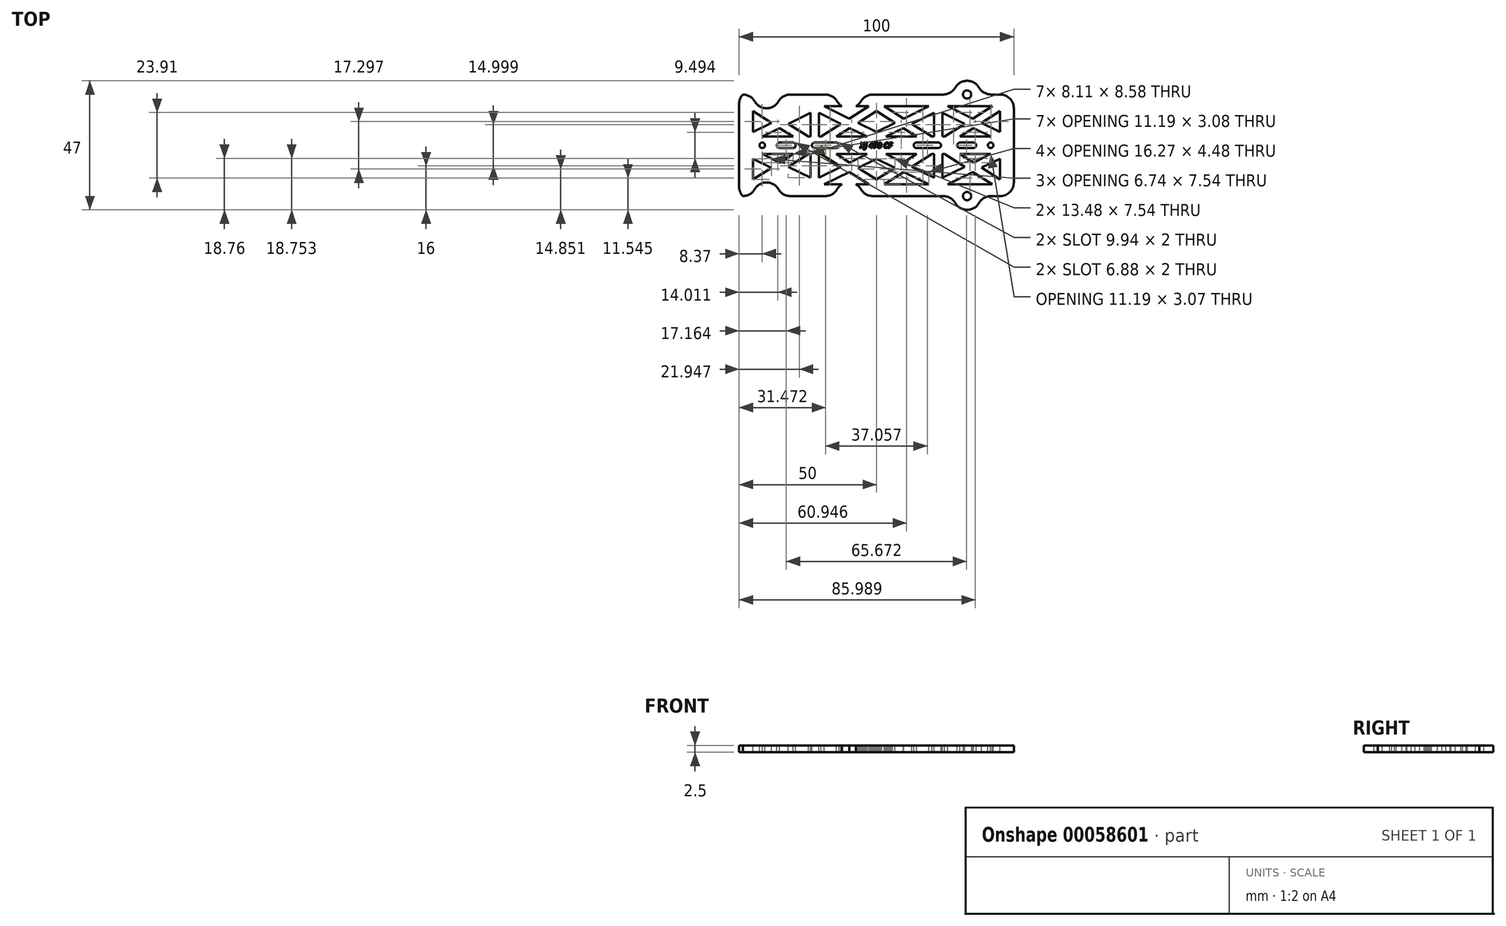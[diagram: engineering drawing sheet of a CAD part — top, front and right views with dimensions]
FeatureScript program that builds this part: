
annotation { "Feature Type Name" : "Feature", "Feature Type Description" : "" }
export const myFeature = defineFeature(function(context is Context, id is Id, definition is map)
    precondition{}
    {
        {
            var Q0;
            Q0=qCreatedBy(makeId("Top.planeOp"),FACE);
            var sketch = newSketch(context, id + "F0", { "sketchPlane" : qUnion([Q0])});
            skLineSegment(sketch, "E0.bottom", {"start": v(-50, 18.5) * mm, "end": v(50, 18.5) * mm});
            skLineSegment(sketch, "E0.top", {"start": v(-50, -18.5) * mm, "end": v(50, -18.5) * mm});
            skLineSegment(sketch, "E0.left", {"start": v(-50, 18.5) * mm, "end": v(-50, -18.5) * mm});
            skLineSegment(sketch, "E0.right", {"start": v(50, 18.5) * mm, "end": v(50, -18.5) * mm});
            skCircle(sketch, "E1", {"center": v(-40, 18.5) * mm, "radius": 5 * mm});
            skCircle(sketch, "E2", {"center": v(-10, 18.5) * mm, "radius": 5 * mm});
            skCircle(sketch, "E3", {"center": v(33, 18.5) * mm, "radius": 5 * mm});
            skCircle(sketch, "E4", {"center": v(-40, 18.5) * mm, "radius": 1.5 * mm});
            skCircle(sketch, "E5", {"center": v(-10, 18.5) * mm, "radius": 1.5 * mm});
            skCircle(sketch, "E6", {"center": v(33, 18.5) * mm, "radius": 1.5 * mm});
            skCircle(sketch, "E7.MirrorC", {"center": v(-40, -18.5) * mm, "radius": 5 * mm});
            skCircle(sketch, "E8.MirrorC", {"center": v(-10, -18.5) * mm, "radius": 5 * mm});
            skCircle(sketch, "E9.MirrorC", {"center": v(33, -18.5) * mm, "radius": 1.5 * mm});
            skCircle(sketch, "E10.MirrorC", {"center": v(-10, -18.5) * mm, "radius": 1.5 * mm});
            skCircle(sketch, "E11.MirrorC", {"center": v(-40, -18.5) * mm, "radius": 1.5 * mm});
            skCircle(sketch, "E12.MirrorC", {"center": v(33, -18.5) * mm, "radius": 5 * mm});
            skSolve(sketch);
        }
        {
            var Q0;
            {var subQ0=sQuery(id+"F0.wireOp",EDGE,"E0.left");Q0=makeQuery(id+"F0.imprint","IMPRINT",FACE,{"disambiguationData":[TD([[makeQuery(id+"F0.imprint","IMPRINT",EDGE,{"derivedFrom":subQ0}),1.0]])]});}
            var Q1;
            {var subQ0=sQuery(id+"F0.wireOp",EDGE,"E1");var subQ1=sQuery(id+"F0.wireOp",EDGE,"E0.bottom");var subQ2=makeQuery(id+"F0.imprint","INTERSECT",VERTEX,{"disambiguationData":[OD(0.0)],"derivedFrom":[subQ1,subQ0]});Q1=makeQuery(id+"F0.imprint","IMPRINT",FACE,{"disambiguationData":[TD([[makeQuery(id+"F0.imprint","IMPRINT",EDGE,{"disambiguationData":[TD([[subQ2,-1.0]])],"derivedFrom":subQ1}),-1.0]])]});}
            var Q2;
            {var subQ0=sQuery(id+"F0.wireOp",EDGE,"E1");var subQ1=sQuery(id+"F0.wireOp",EDGE,"E0.bottom");var subQ2=makeQuery(id+"F0.imprint","INTERSECT",VERTEX,{"disambiguationData":[OD(0.0)],"derivedFrom":[subQ1,subQ0]});Q2=makeQuery(id+"F0.imprint","IMPRINT",FACE,{"disambiguationData":[TD([[makeQuery(id+"F0.imprint","IMPRINT",EDGE,{"disambiguationData":[TD([[subQ2,-1.0]])],"derivedFrom":subQ1}),1.0]])]});}
            var Q3;
            {var subQ0=sQuery(id+"F0.wireOp",EDGE,"E2");var subQ1=sQuery(id+"F0.wireOp",EDGE,"E0.bottom");var subQ2=makeQuery(id+"F0.imprint","INTERSECT",VERTEX,{"disambiguationData":[OD(0.0)],"derivedFrom":[subQ1,subQ0]});Q3=makeQuery(id+"F0.imprint","IMPRINT",FACE,{"disambiguationData":[TD([[makeQuery(id+"F0.imprint","IMPRINT",EDGE,{"disambiguationData":[TD([[subQ2,-1.0]])],"derivedFrom":subQ1}),1.0]])]});}
            var Q4;
            {var subQ0=sQuery(id+"F0.wireOp",EDGE,"E2");var subQ1=sQuery(id+"F0.wireOp",EDGE,"E0.bottom");var subQ2=makeQuery(id+"F0.imprint","INTERSECT",VERTEX,{"disambiguationData":[OD(0.0)],"derivedFrom":[subQ1,subQ0]});Q4=makeQuery(id+"F0.imprint","IMPRINT",FACE,{"disambiguationData":[TD([[makeQuery(id+"F0.imprint","IMPRINT",EDGE,{"disambiguationData":[TD([[subQ2,-1.0]])],"derivedFrom":subQ1}),-1.0]])]});}
            var Q5;
            {var subQ0=sQuery(id+"F0.wireOp",EDGE,"E3");var subQ1=sQuery(id+"F0.wireOp",EDGE,"E0.bottom");var subQ2=makeQuery(id+"F0.imprint","INTERSECT",VERTEX,{"disambiguationData":[OD(0.0)],"derivedFrom":[subQ1,subQ0]});Q5=makeQuery(id+"F0.imprint","IMPRINT",FACE,{"disambiguationData":[TD([[makeQuery(id+"F0.imprint","IMPRINT",EDGE,{"disambiguationData":[TD([[subQ2,-1.0]])],"derivedFrom":subQ1}),1.0]])]});}
            var Q6;
            {var subQ0=sQuery(id+"F0.wireOp",EDGE,"E3");var subQ1=sQuery(id+"F0.wireOp",EDGE,"E0.bottom");var subQ2=makeQuery(id+"F0.imprint","INTERSECT",VERTEX,{"disambiguationData":[OD(0.0)],"derivedFrom":[subQ1,subQ0]});Q6=makeQuery(id+"F0.imprint","IMPRINT",FACE,{"disambiguationData":[TD([[makeQuery(id+"F0.imprint","IMPRINT",EDGE,{"disambiguationData":[TD([[subQ2,-1.0]])],"derivedFrom":subQ1}),-1.0]])]});}
            var Q7;
            {var subQ0=sQuery(id+"F0.wireOp",EDGE,"E12.MirrorC");var subQ1=sQuery(id+"F0.wireOp",EDGE,"E0.top");var subQ2=makeQuery(id+"F0.imprint","INTERSECT",VERTEX,{"disambiguationData":[OD(0.0)],"derivedFrom":[subQ1,subQ0]});Q7=makeQuery(id+"F0.imprint","IMPRINT",FACE,{"disambiguationData":[TD([[makeQuery(id+"F0.imprint","IMPRINT",EDGE,{"disambiguationData":[TD([[subQ2,-1.0]])],"derivedFrom":subQ1}),-1.0]])]});}
            var Q8;
            {var subQ0=sQuery(id+"F0.wireOp",EDGE,"E12.MirrorC");var subQ1=sQuery(id+"F0.wireOp",EDGE,"E0.top");var subQ2=makeQuery(id+"F0.imprint","INTERSECT",VERTEX,{"disambiguationData":[OD(0.0)],"derivedFrom":[subQ1,subQ0]});Q8=makeQuery(id+"F0.imprint","IMPRINT",FACE,{"disambiguationData":[TD([[makeQuery(id+"F0.imprint","IMPRINT",EDGE,{"disambiguationData":[TD([[subQ2,-1.0]])],"derivedFrom":subQ1}),1.0]])]});}
            var Q9;
            {var subQ0=sQuery(id+"F0.wireOp",EDGE,"E8.MirrorC");var subQ1=sQuery(id+"F0.wireOp",EDGE,"E0.top");var subQ2=makeQuery(id+"F0.imprint","INTERSECT",VERTEX,{"disambiguationData":[OD(0.0)],"derivedFrom":[subQ1,subQ0]});Q9=makeQuery(id+"F0.imprint","IMPRINT",FACE,{"disambiguationData":[TD([[makeQuery(id+"F0.imprint","IMPRINT",EDGE,{"disambiguationData":[TD([[subQ2,-1.0]])],"derivedFrom":subQ1}),1.0]])]});}
            var Q10;
            {var subQ0=sQuery(id+"F0.wireOp",EDGE,"E8.MirrorC");var subQ1=sQuery(id+"F0.wireOp",EDGE,"E0.top");var subQ2=makeQuery(id+"F0.imprint","INTERSECT",VERTEX,{"disambiguationData":[OD(0.0)],"derivedFrom":[subQ1,subQ0]});Q10=makeQuery(id+"F0.imprint","IMPRINT",FACE,{"disambiguationData":[TD([[makeQuery(id+"F0.imprint","IMPRINT",EDGE,{"disambiguationData":[TD([[subQ2,-1.0]])],"derivedFrom":subQ1}),-1.0]])]});}
            var Q11;
            {var subQ0=sQuery(id+"F0.wireOp",EDGE,"E7.MirrorC");var subQ1=sQuery(id+"F0.wireOp",EDGE,"E0.top");var subQ2=makeQuery(id+"F0.imprint","INTERSECT",VERTEX,{"disambiguationData":[OD(0.0)],"derivedFrom":[subQ1,subQ0]});Q11=makeQuery(id+"F0.imprint","IMPRINT",FACE,{"disambiguationData":[TD([[makeQuery(id+"F0.imprint","IMPRINT",EDGE,{"disambiguationData":[TD([[subQ2,-1.0]])],"derivedFrom":subQ1}),-1.0]])]});}
            var Q12;
            {var subQ0=sQuery(id+"F0.wireOp",EDGE,"E7.MirrorC");var subQ1=sQuery(id+"F0.wireOp",EDGE,"E0.top");var subQ2=makeQuery(id+"F0.imprint","INTERSECT",VERTEX,{"disambiguationData":[OD(0.0)],"derivedFrom":[subQ1,subQ0]});Q12=makeQuery(id+"F0.imprint","IMPRINT",FACE,{"disambiguationData":[TD([[makeQuery(id+"F0.imprint","IMPRINT",EDGE,{"disambiguationData":[TD([[subQ2,-1.0]])],"derivedFrom":subQ1}),1.0]])]});}
            extrude(context, id + "F1", {"entities" : qUnion([Q0, Q1, Q2, Q3, Q4, Q5, Q6, Q7, Q8, Q9, Q10, Q11, Q12]), "depth" : 2.5 * mm});
        }
        {
            var Q0;
            {var subQ0=sQuery(id+"F0.wireOp",EDGE,"E7.MirrorC");var subQ1=sQuery(id+"F0.wireOp",EDGE,"E0.top");Q0=makeQuery(id+"F1.opExtrude","SWEPT_EDGE",EDGE,{"disambiguationData":[OSD([subQ1,subQ0]),TDD([makeQuery(id+"F0.imprint","INTERSECT",VERTEX,{"disambiguationData":[OD(1.0)],"derivedFrom":[subQ1,subQ0]})])]});}
            var Q1;
            {var subQ0=sQuery(id+"F0.wireOp",EDGE,"E8.MirrorC");var subQ1=sQuery(id+"F0.wireOp",EDGE,"E0.top");Q1=makeQuery(id+"F1.opExtrude","SWEPT_EDGE",EDGE,{"disambiguationData":[OSD([subQ1,subQ0]),TDD([makeQuery(id+"F0.imprint","INTERSECT",VERTEX,{"disambiguationData":[OD(1.0)],"derivedFrom":[subQ1,subQ0]})])]});}
            var Q2;
            {var subQ0=sQuery(id+"F0.wireOp",EDGE,"E12.MirrorC");var subQ1=sQuery(id+"F0.wireOp",EDGE,"E0.top");Q2=makeQuery(id+"F1.opExtrude","SWEPT_EDGE",EDGE,{"disambiguationData":[OSD([subQ1,subQ0]),TDD([makeQuery(id+"F0.imprint","INTERSECT",VERTEX,{"disambiguationData":[OD(1.0)],"derivedFrom":[subQ1,subQ0]})])]});}
            var Q3;
            Q3=makeQuery(id+"F1.opExtrude","SWEPT_EDGE",EDGE,{"disambiguationData":[OSD([sQuery(id+"F0.wireOp",EDGE,"E0.top"),sQuery(id+"F0.wireOp",EDGE,"E0.right")])]});
            var Q4;
            Q4=makeQuery(id+"F1.opExtrude","SWEPT_EDGE",EDGE,{"disambiguationData":[OSD([sQuery(id+"F0.wireOp",EDGE,"E0.bottom"),sQuery(id+"F0.wireOp",EDGE,"E0.right")])]});
            var Q5;
            {var subQ0=sQuery(id+"F0.wireOp",EDGE,"E7.MirrorC");var subQ1=sQuery(id+"F0.wireOp",EDGE,"E0.top");Q5=makeQuery(id+"F1.opExtrude","SWEPT_EDGE",EDGE,{"disambiguationData":[OSD([subQ1,subQ0]),TDD([makeQuery(id+"F0.imprint","INTERSECT",VERTEX,{"disambiguationData":[OD(0.0)],"derivedFrom":[subQ1,subQ0]})])]});}
            var Q6;
            {var subQ0=sQuery(id+"F0.wireOp",EDGE,"E8.MirrorC");var subQ1=sQuery(id+"F0.wireOp",EDGE,"E0.top");Q6=makeQuery(id+"F1.opExtrude","SWEPT_EDGE",EDGE,{"disambiguationData":[OSD([subQ1,subQ0]),TDD([makeQuery(id+"F0.imprint","INTERSECT",VERTEX,{"disambiguationData":[OD(0.0)],"derivedFrom":[subQ1,subQ0]})])]});}
            var Q7;
            {var subQ0=sQuery(id+"F0.wireOp",EDGE,"E12.MirrorC");var subQ1=sQuery(id+"F0.wireOp",EDGE,"E0.top");Q7=makeQuery(id+"F1.opExtrude","SWEPT_EDGE",EDGE,{"disambiguationData":[OSD([subQ1,subQ0]),TDD([makeQuery(id+"F0.imprint","INTERSECT",VERTEX,{"disambiguationData":[OD(0.0)],"derivedFrom":[subQ1,subQ0]})])]});}
            var Q8;
            {var subQ0=sQuery(id+"F0.wireOp",EDGE,"E3");var subQ1=sQuery(id+"F0.wireOp",EDGE,"E0.bottom");Q8=makeQuery(id+"F1.opExtrude","SWEPT_EDGE",EDGE,{"disambiguationData":[OSD([subQ1,subQ0]),TDD([makeQuery(id+"F0.imprint","INTERSECT",VERTEX,{"disambiguationData":[OD(0.0)],"derivedFrom":[subQ1,subQ0]})])]});}
            var Q9;
            {var subQ0=sQuery(id+"F0.wireOp",EDGE,"E2");var subQ1=sQuery(id+"F0.wireOp",EDGE,"E0.bottom");Q9=makeQuery(id+"F1.opExtrude","SWEPT_EDGE",EDGE,{"disambiguationData":[OSD([subQ1,subQ0]),TDD([makeQuery(id+"F0.imprint","INTERSECT",VERTEX,{"disambiguationData":[OD(0.0)],"derivedFrom":[subQ1,subQ0]})])]});}
            var Q10;
            {var subQ0=sQuery(id+"F0.wireOp",EDGE,"E1");var subQ1=sQuery(id+"F0.wireOp",EDGE,"E0.bottom");Q10=makeQuery(id+"F1.opExtrude","SWEPT_EDGE",EDGE,{"disambiguationData":[OSD([subQ1,subQ0]),TDD([makeQuery(id+"F0.imprint","INTERSECT",VERTEX,{"disambiguationData":[OD(0.0)],"derivedFrom":[subQ1,subQ0]})])]});}
            var Q11;
            {var subQ0=sQuery(id+"F0.wireOp",EDGE,"E3");var subQ1=sQuery(id+"F0.wireOp",EDGE,"E0.bottom");Q11=makeQuery(id+"F1.opExtrude","SWEPT_EDGE",EDGE,{"disambiguationData":[OSD([subQ1,subQ0]),TDD([makeQuery(id+"F0.imprint","INTERSECT",VERTEX,{"disambiguationData":[OD(1.0)],"derivedFrom":[subQ1,subQ0]})])]});}
            var Q12;
            {var subQ0=sQuery(id+"F0.wireOp",EDGE,"E2");var subQ1=sQuery(id+"F0.wireOp",EDGE,"E0.bottom");Q12=makeQuery(id+"F1.opExtrude","SWEPT_EDGE",EDGE,{"disambiguationData":[OSD([subQ1,subQ0]),TDD([makeQuery(id+"F0.imprint","INTERSECT",VERTEX,{"disambiguationData":[OD(1.0)],"derivedFrom":[subQ1,subQ0]})])]});}
            var Q13;
            {var subQ0=sQuery(id+"F0.wireOp",EDGE,"E1");var subQ1=sQuery(id+"F0.wireOp",EDGE,"E0.bottom");Q13=makeQuery(id+"F1.opExtrude","SWEPT_EDGE",EDGE,{"disambiguationData":[OSD([subQ1,subQ0]),TDD([makeQuery(id+"F0.imprint","INTERSECT",VERTEX,{"disambiguationData":[OD(1.0)],"derivedFrom":[subQ1,subQ0]})])]});}
            fillet(context, id + "F2", {"entities" : qUnion([Q0, Q1, Q2, Q3, Q4, Q5, Q6, Q7, Q8, Q9, Q10, Q11, Q12, Q13]), "radius" : 5 * mm, "tangentPropagation" : true, "allowEdgeOverflow" : false});
        }
        {
            var Q0;
            Q0=makeQuery(id+"F1.opExtrude","SWEPT_EDGE",EDGE,{"disambiguationData":[OSD([sQuery(id+"F0.wireOp",EDGE,"E0.bottom"),sQuery(id+"F0.wireOp",EDGE,"E0.left")])]});
            var Q1;
            Q1=makeQuery(id+"F1.opExtrude","SWEPT_EDGE",EDGE,{"disambiguationData":[OSD([sQuery(id+"F0.wireOp",EDGE,"E0.top"),sQuery(id+"F0.wireOp",EDGE,"E0.left")])]});
            fillet(context, id + "F3", {"entities" : qUnion([Q0, Q1]), "radius" : 5 * mm, "tangentPropagation" : true, "allowEdgeOverflow" : false});
        }
        {
            var Q0;
            Q0=makeQuery(id+"F1.opExtrude","CAP_FACE",FACE,{"disambiguationData":[OSD([sQuery(id+"F0.wireOp",EDGE,"E0.bottom"),sQuery(id+"F0.wireOp",EDGE,"E0.top"),sQuery(id+"F0.wireOp",EDGE,"E0.left"),sQuery(id+"F0.wireOp",EDGE,"E0.right"),sQuery(id+"F0.wireOp",EDGE,"E1"),sQuery(id+"F0.wireOp",EDGE,"E2"),sQuery(id+"F0.wireOp",EDGE,"E3"),sQuery(id+"F0.wireOp",EDGE,"E4"),sQuery(id+"F0.wireOp",EDGE,"E5"),sQuery(id+"F0.wireOp",EDGE,"E6"),sQuery(id+"F0.wireOp",EDGE,"E7.MirrorC"),sQuery(id+"F0.wireOp",EDGE,"E8.MirrorC"),sQuery(id+"F0.wireOp",EDGE,"E9.MirrorC"),sQuery(id+"F0.wireOp",EDGE,"E10.MirrorC"),sQuery(id+"F0.wireOp",EDGE,"E11.MirrorC"),sQuery(id+"F0.wireOp",EDGE,"E12.MirrorC")])],"isStart":false});
            var sketch = newSketch(context, id + "F4", { "sketchPlane" : qUnion([Q0])});
            skLineSegment(sketch, "E13", {"start": v(-45, -14.2) * mm, "end": v(45, -14.2) * mm});
            skLineSegment(sketch, "E14", {"start": v(45, -14.2) * mm, "end": v(45, 14.2) * mm});
            skLineSegment(sketch, "E15", {"start": v(45, 14.2) * mm, "end": v(-45, 14.2) * mm});
            skLineSegment(sketch, "E16", {"start": v(-45, 14.2) * mm, "end": v(-45, -14.2) * mm});
            skLineSegment(sketch, "E17", {"start": v(-41.58, 3.2) * mm, "end": v(-30.4, 3.2) * mm});
            skLineSegment(sketch, "E18", {"start": v(-41.58, -3.2) * mm, "end": v(-30.4, -3.2) * mm});
            skLineSegment(sketch, "E19.0.left", {"start": v(-42.19, 14.2) * mm, "end": v(-35.09, 9.72) * mm});
            skLineSegment(sketch, "E19.0.right", {"start": v(-45, 12.42) * mm, "end": v(-38.26, 8.17) * mm});
            skLineSegment(sketch, "E19.1.left", {"start": v(2.81, 14.2) * mm, "end": v(9.91, 9.72) * mm});
            skLineSegment(sketch, "E19.1.right", {"start": v(0, 12.42) * mm, "end": v(6.74, 8.17) * mm});
            skLineSegment(sketch, "E19.2.left", {"start": v(-45, -12.42) * mm, "end": v(-38.26, -8.17) * mm});
            skLineSegment(sketch, "E19.2.right", {"start": v(-42.19, -14.2) * mm, "end": v(-35.09, -9.72) * mm});
            skLineSegment(sketch, "E19.3.left", {"start": v(0, -12.42) * mm, "end": v(6.74, -8.17) * mm});
            skLineSegment(sketch, "E19.3.right", {"start": v(2.81, -14.2) * mm, "end": v(9.91, -9.72) * mm});
            skPoint(sketch, "E20.endSnap0", {"position": v(22.5, 0) * mm});
            skLineSegment(sketch, "E21.0.left", {"start": v(-45, 4.88) * mm, "end": v(-38.26, 8.17) * mm});
            skLineSegment(sketch, "E21.0.right", {"start": v(-41.58, 3.2) * mm, "end": v(-35.28, 6.29) * mm});
            skLineSegment(sketch, "E21.1.left", {"start": v(-19.08, 14.2) * mm, "end": v(-9.91, 9.72) * mm});
            skLineSegment(sketch, "E21.2.left", {"start": v(0, 4.88) * mm, "end": v(6.74, 8.17) * mm});
            skLineSegment(sketch, "E21.2.right", {"start": v(3.42, 3.2) * mm, "end": v(9.72, 6.29) * mm});
            skLineSegment(sketch, "E21.3.left", {"start": v(25.92, 14.2) * mm, "end": v(35.09, 9.72) * mm});
            skLineSegment(sketch, "E21.3.right", {"start": v(24, 11.8) * mm, "end": v(32.1, 7.83) * mm});
            skLineSegment(sketch, "E21.4.left", {"start": v(24, -11.76) * mm, "end": v(32.09, -7.82) * mm});
            skLineSegment(sketch, "E21.4.right", {"start": v(25.92, -14.2) * mm, "end": v(35.09, -9.72) * mm});
            skLineSegment(sketch, "E21.5.left", {"start": v(3.42, -3.2) * mm, "end": v(9.72, -6.29) * mm});
            skLineSegment(sketch, "E21.5.right", {"start": v(0, -4.88) * mm, "end": v(6.74, -8.17) * mm});
            skLineSegment(sketch, "E21.6.right", {"start": v(-19.08, -14.2) * mm, "end": v(-9.91, -9.72) * mm});
            skLineSegment(sketch, "E21.7.left", {"start": v(-41.58, -3.2) * mm, "end": v(-35.28, -6.29) * mm});
            skLineSegment(sketch, "E21.7.right", {"start": v(-45, -4.88) * mm, "end": v(-38.26, -8.17) * mm});
            skLineSegment(sketch, "E22.0.left", {"start": v(-21, 11.8) * mm, "end": v(-21, 3.2) * mm});
            skLineSegment(sketch, "E22.1.left", {"start": v(24, 11.8) * mm, "end": v(24, 3.2) * mm});
            skLineSegment(sketch, "E22.1.right", {"start": v(21, 11.8) * mm, "end": v(21, 3.2) * mm});
            skLineSegment(sketch, "E23.trimOffspring", {"start": v(-35.28, 6.29) * mm, "end": v(-30.4, 3.2) * mm});
            skLineSegment(sketch, "E24.trimOffspring", {"start": v(-32.1, 7.83) * mm, "end": v(-24.77, 3.2) * mm});
            skLineSegment(sketch, "E25.trimOffspring", {"start": v(-35.09, 9.72) * mm, "end": v(-25.92, 14.2) * mm});
            skPoint(sketch, "E21.0.startCap.center.orphan", {"position": v(-45, 3.2) * mm});
            skLineSegment(sketch, "E26.trimOffspring", {"start": v(-32.1, 7.83) * mm, "end": v(-24, 11.8) * mm});
            skLineSegment(sketch, "E27.trimOffspring", {"start": v(-24, 11.8) * mm, "end": v(-24, 3.2) * mm});
            skLineSegment(sketch, "E28.trimOffspring", {"start": v(-21, 11.8) * mm, "end": v(-12.9, 7.83) * mm});
            skLineSegment(sketch, "E29.trimOffspring", {"start": v(-24.77, 3.2) * mm, "end": v(-24, 3.2) * mm});
            skLineSegment(sketch, "E30.trimOffspring", {"start": v(-14.6, -3.2) * mm, "end": v(-9.72, -6.29) * mm});
            skLineSegment(sketch, "E31.trimOffspring", {"start": v(-21, 3.2) * mm, "end": v(-20.23, 3.2) * mm});
            skPoint(sketch, "E32.orphan", {"position": v(-22.5, 14.2) * mm});
            skLineSegment(sketch, "E33.trimOffspring", {"start": v(-9.91, 9.72) * mm, "end": v(-2.81, 14.2) * mm});
            skLineSegment(sketch, "E34.trimOffspring", {"start": v(-6.74, 8.17) * mm, "end": v(0, 12.42) * mm});
            skLineSegment(sketch, "E35.trimOffspring", {"start": v(-6.74, 8.17) * mm, "end": v(0, 4.88) * mm});
            skLineSegment(sketch, "E36.trimOffspring", {"start": v(-9.72, 6.29) * mm, "end": v(-3.42, 3.2) * mm});
            skLineSegment(sketch, "E37.trimOffspring", {"start": v(-14.6, 3.2) * mm, "end": v(-3.42, 3.2) * mm});
            skLineSegment(sketch, "E38.trimOffspring", {"start": v(-21, -3.2) * mm, "end": v(-21, -11.8) * mm});
            skLineSegment(sketch, "E39.trimOffspring", {"start": v(-20.23, 3.2) * mm, "end": v(-12.9, 7.83) * mm});
            skPoint(sketch, "E40.orphan", {"position": v(0, 14.2) * mm});
            skLineSegment(sketch, "E41.trimOffspring", {"start": v(-14.6, 3.2) * mm, "end": v(-9.72, 6.29) * mm});
            skLineSegment(sketch, "E42.trimOffspring", {"start": v(3.42, 3.2) * mm, "end": v(14.6, 3.2) * mm});
            skPoint(sketch, "E21.2.startCap.center.orphan", {"position": v(0, 3.2) * mm});
            skLineSegment(sketch, "E43.trimOffspring", {"start": v(9.72, 6.29) * mm, "end": v(14.6, 3.2) * mm});
            skLineSegment(sketch, "E44.trimOffspring", {"start": v(9.91, 9.72) * mm, "end": v(19.08, 14.2) * mm});
            skLineSegment(sketch, "E45.trimOffspring", {"start": v(12.9, 7.83) * mm, "end": v(20.23, 3.2) * mm});
            skLineSegment(sketch, "E46.trimOffspring", {"start": v(-32.1, -7.83) * mm, "end": v(-24, -11.8) * mm});
            skLineSegment(sketch, "E47.trimOffspring", {"start": v(-35.28, -6.29) * mm, "end": v(-30.4, -3.2) * mm});
            skLineSegment(sketch, "E48.trimOffspring", {"start": v(-32.1, -7.83) * mm, "end": v(-24.77, -3.2) * mm});
            skLineSegment(sketch, "E49.trimOffspring", {"start": v(-35.09, -9.72) * mm, "end": v(-25.92, -14.2) * mm});
            skPoint(sketch, "E21.7.startCap.center.orphan", {"position": v(-45, -3.2) * mm});
            skLineSegment(sketch, "E50.trimOffspring", {"start": v(-24.77, -3.2) * mm, "end": v(-24, -3.2) * mm});
            skLineSegment(sketch, "E51.trimOffspring", {"start": v(-24, -3.2) * mm, "end": v(-24, -11.8) * mm});
            skLineSegment(sketch, "E52.trimOffspring", {"start": v(-20.23, -3.2) * mm, "end": v(-12.9, -7.83) * mm});
            skLineSegment(sketch, "E53.trimOffspring", {"start": v(-21, -3.2) * mm, "end": v(-20.23, -3.2) * mm});
            skLineSegment(sketch, "E54.trimOffspring", {"start": v(-21, -11.8) * mm, "end": v(-12.9, -7.83) * mm});
            skPoint(sketch, "E55.trimOffspring.end.orphan", {"position": v(-22.5, -14.2) * mm});
            skLineSegment(sketch, "E56.trimOffspring", {"start": v(-14.6, -3.2) * mm, "end": v(-3.42, -3.2) * mm});
            skLineSegment(sketch, "E57.trimOffspring", {"start": v(3.42, -3.2) * mm, "end": v(14.6, -3.2) * mm});
            skPoint(sketch, "E58.orphan", {"position": v(0, -3.2) * mm});
            skLineSegment(sketch, "E59.trimOffspring", {"start": v(-9.72, -6.29) * mm, "end": v(-3.42, -3.2) * mm});
            skLineSegment(sketch, "E60.trimOffspring", {"start": v(-6.74, -8.17) * mm, "end": v(0, -12.42) * mm});
            skLineSegment(sketch, "E61.trimOffspring", {"start": v(-9.91, -9.72) * mm, "end": v(-2.81, -14.2) * mm});
            skLineSegment(sketch, "E62.trimOffspring", {"start": v(-6.74, -8.17) * mm, "end": v(0, -4.88) * mm});
            skPoint(sketch, "E63.orphan", {"position": v(0, -14.2) * mm});
            skPoint(sketch, "E64.orphan", {"position": v(22.5, 14.2) * mm});
            skLineSegment(sketch, "E65.trimOffspring", {"start": v(12.9, 7.83) * mm, "end": v(21, 11.8) * mm});
            skLineSegment(sketch, "E66.trimOffspring", {"start": v(20.23, 3.2) * mm, "end": v(21, 3.2) * mm});
            skLineSegment(sketch, "E67.trimOffspring", {"start": v(24.77, 3.2) * mm, "end": v(32.1, 7.83) * mm});
            skLineSegment(sketch, "E68.trimOffspring", {"start": v(24, 3.2) * mm, "end": v(24.77, 3.2) * mm});
            skLineSegment(sketch, "E69.trimOffspring", {"start": v(30.4, 3.2) * mm, "end": v(41.58, 3.2) * mm});
            skLineSegment(sketch, "E70.trimOffspring", {"start": v(21, -3.2) * mm, "end": v(21, -11.8) * mm});
            skLineSegment(sketch, "E71.trimOffspring", {"start": v(30.4, -3.2) * mm, "end": v(35.28, -6.27) * mm});
            skLineSegment(sketch, "E72.trimOffspring", {"start": v(30.4, 3.2) * mm, "end": v(35.28, 6.29) * mm});
            skLineSegment(sketch, "E73.trimOffspring", {"start": v(24.77, -3.2) * mm, "end": v(32.09, -7.82) * mm});
            skLineSegment(sketch, "E74", {"start": v(9.72, -6.29) * mm, "end": v(14.6, -3.2) * mm});
            skLineSegment(sketch, "E75.trimOffspring", {"start": v(20.23, -3.2) * mm, "end": v(21, -3.2) * mm});
            skLineSegment(sketch, "E76.trimOffspring", {"start": v(12.9, -7.83) * mm, "end": v(21, -11.8) * mm});
            skLineSegment(sketch, "E77.trimOffspring", {"start": v(9.91, -9.72) * mm, "end": v(19.08, -14.2) * mm});
            skLineSegment(sketch, "E78.trimOffspring", {"start": v(12.9, -7.83) * mm, "end": v(20.23, -3.2) * mm});
            skLineSegment(sketch, "E79.trimOffspring", {"start": v(24, -3.2) * mm, "end": v(24, -11.76) * mm});
            skLineSegment(sketch, "E80.trimOffspring", {"start": v(24, -3.2) * mm, "end": v(24.77, -3.2) * mm});
            skPoint(sketch, "E21.5.endCap.center.orphan", {"position": v(22.5, -14.2) * mm});
            skLineSegment(sketch, "E81.trimOffspring", {"start": v(35.09, -9.72) * mm, "end": v(42.19, -14.2) * mm});
            skLineSegment(sketch, "E82.trimOffspring", {"start": v(35.28, -6.27) * mm, "end": v(41.58, -3.2) * mm});
            skLineSegment(sketch, "E83.trimOffspring", {"start": v(30.4, -3.2) * mm, "end": v(41.58, -3.2) * mm});
            skPoint(sketch, "E21.3.endCap.center.orphan", {"position": v(45, 3.2) * mm});
            skLineSegment(sketch, "E84.trimOffspring", {"start": v(38.26, 8.17) * mm, "end": v(45, 12.42) * mm});
            skLineSegment(sketch, "E85.trimOffspring", {"start": v(35.09, 9.72) * mm, "end": v(42.19, 14.2) * mm});
            skLineSegment(sketch, "E86.trimOffspring", {"start": v(35.28, 6.29) * mm, "end": v(41.58, 3.2) * mm});
            skLineSegment(sketch, "E87.trimOffspring", {"start": v(38.26, 8.17) * mm, "end": v(45, 4.88) * mm});
            skLineSegment(sketch, "E88.trimOffspring", {"start": v(38.28, -8.16) * mm, "end": v(45, -4.88) * mm});
            skLineSegment(sketch, "E89.trimOffspring", {"start": v(38.28, -8.16) * mm, "end": v(45, -12.38) * mm});
            skPoint(sketch, "E21.4.endCap.center.orphan", {"position": v(45, -3.2) * mm});
            skText(sketch, "E90", { "text": "XJ 470 CF", "fontName": "OpenSans-BoldItalic.ttf"});
            skLineSegment(sketch, "E91.bottom", {"start": v(14.56, 1) * mm, "end": v(22.5, 1) * mm});
            skArc(sketch, "E92", {"start": v(14.56, 1) * mm, "mid": v(13.56, 0) * mm, "end": v(14.56, -1) * mm});
            skArc(sketch, "E93", {"start": v(35.28, -1) * mm, "mid": v(36.28, 0) * mm, "end": v(35.28, 1) * mm});
            skArc(sketch, "E94", {"start": v(22.5, -1) * mm, "mid": v(23.5, 0) * mm, "end": v(22.5, 1) * mm});
            skArc(sketch, "E95", {"start": v(30.4, 1) * mm, "mid": v(29.4, 0) * mm, "end": v(30.4, -1) * mm});
            skLineSegment(sketch, "E96.trimOffspring", {"start": v(30.4, 1) * mm, "end": v(35.28, 1) * mm});
            skLineSegment(sketch, "E97.trimOffspring", {"start": v(30.4, -1) * mm, "end": v(35.28, -1) * mm});
            skLineSegment(sketch, "E98", {"start": v(14.56, -1) * mm, "end": v(22.5, -1) * mm});
            skLineSegment(sketch, "E99.MirrorCS", {"start": v(-30.4, -1) * mm, "end": v(-35.28, -1) * mm});
            skLineSegment(sketch, "E100.MirrorCS", {"start": v(-14.56, -1) * mm, "end": v(-22.5, -1) * mm});
            skArc(sketch, "E101.MirrorCS", {"start": v(-30.4, 1) * mm, "mid": v(-29.4, 0) * mm, "end": v(-30.4, -1) * mm});
            skArc(sketch, "E102.MirrorCS", {"start": v(-35.28, -1) * mm, "mid": v(-36.28, 0) * mm, "end": v(-35.28, 1) * mm});
            skLineSegment(sketch, "E103.MirrorCS", {"start": v(-30.4, 1) * mm, "end": v(-35.28, 1) * mm});
            skLineSegment(sketch, "E104.MirrorCS", {"start": v(-14.56, 1) * mm, "end": v(-22.5, 1) * mm});
            skArc(sketch, "E105.MirrorCS", {"start": v(-22.5, -1) * mm, "mid": v(-23.5, 0) * mm, "end": v(-22.5, 1) * mm});
            skArc(sketch, "E106.MirrorCS", {"start": v(-14.56, 1) * mm, "mid": v(-13.56, 0) * mm, "end": v(-14.56, -1) * mm});
            skCircle(sketch, "E107", {"center": v(41.58, 0) * mm, "radius": 1 * mm});
            skCircle(sketch, "E108", {"center": v(-41.58, 0) * mm, "radius": 1 * mm});
            const initialGuessF4  = {"E90": [-0.00604, -0.001, 1, 0, 0.002]};
            skSetInitialGuess(sketch, initialGuessF4);
            skSolve(sketch);
        }
        {
            var Q0;
            {var subQ0=sQuery(id+"F4.wireOp",EDGE,"E19.0.right");Q0=makeQuery(id+"F4.imprint","IMPRINT",FACE,{"disambiguationData":[TD([[makeQuery(id+"F4.imprint","IMPRINT",EDGE,{"derivedFrom":subQ0}),-1.0]])]});}
            var Q1;
            {var subQ0=sQuery(id+"F4.wireOp",EDGE,"E19.0.left");Q1=makeQuery(id+"F4.imprint","IMPRINT",FACE,{"disambiguationData":[TD([[makeQuery(id+"F4.imprint","IMPRINT",EDGE,{"derivedFrom":subQ0}),1.0]])]});}
            var Q2;
            Q2=makeQuery(id+"F4.imprint","IMPRINT",FACE,{"disambiguationData":[TD([[makeQuery(id+"F4.imprint","IMPRINT",EDGE,{"derivedFrom":sQuery(id+"F4.wireOp",EDGE,"E24.trimOffspring")}),1.0]])]});
            var Q3;
            Q3=makeQuery(id+"F4.imprint","IMPRINT",FACE,{"disambiguationData":[TD([[makeQuery(id+"F4.imprint","IMPRINT",EDGE,{"derivedFrom":sQuery(id+"F4.wireOp",EDGE,"E17")}),1.0]])]});
            var Q4;
            Q4=makeQuery(id+"F4.imprint","IMPRINT",FACE,{"disambiguationData":[TD([[makeQuery(id+"F4.imprint","IMPRINT",EDGE,{"derivedFrom":sQuery(id+"F4.wireOp",EDGE,"E108")}),1.0]])]});
            var Q5;
            Q5=makeQuery(id+"F4.imprint","IMPRINT",FACE,{"disambiguationData":[TD([[makeQuery(id+"F4.imprint","IMPRINT",EDGE,{"derivedFrom":sQuery(id+"F4.wireOp",EDGE,"E99.MirrorCS")}),-1.0]])]});
            var Q6;
            Q6=makeQuery(id+"F4.imprint","IMPRINT",FACE,{"disambiguationData":[TD([[makeQuery(id+"F4.imprint","IMPRINT",EDGE,{"derivedFrom":sQuery(id+"F4.wireOp",EDGE,"E100.MirrorCS")}),-1.0]])]});
            var Q7;
            Q7=makeQuery(id+"F4.imprint","IMPRINT",FACE,{"disambiguationData":[TD([[makeQuery(id+"F4.imprint","IMPRINT",EDGE,{"derivedFrom":sQuery(id+"F4.wireOp",EDGE,"E22.0.left")}),1.0]])]});
            var Q8;
            Q8=makeQuery(id+"F4.imprint","IMPRINT",FACE,{"disambiguationData":[TD([[makeQuery(id+"F4.imprint","IMPRINT",EDGE,{"derivedFrom":sQuery(id+"F4.wireOp",EDGE,"E36.trimOffspring")}),-1.0]])]});
            var Q9;
            Q9=makeQuery(id+"F4.imprint","IMPRINT",FACE,{"disambiguationData":[TD([[makeQuery(id+"F4.imprint","IMPRINT",EDGE,{"derivedFrom":sQuery(id+"F4.wireOp",EDGE,"E30.trimOffspring")}),1.0]])]});
            var Q10;
            Q10=makeQuery(id+"F4.imprint","IMPRINT",FACE,{"disambiguationData":[TD([[makeQuery(id+"F4.imprint","IMPRINT",EDGE,{"derivedFrom":sQuery(id+"F4.wireOp",EDGE,"E38.trimOffspring")}),1.0]])]});
            var Q11;
            Q11=makeQuery(id+"F4.imprint","IMPRINT",FACE,{"disambiguationData":[TD([[makeQuery(id+"F4.imprint","IMPRINT",EDGE,{"derivedFrom":sQuery(id+"F4.wireOp",EDGE,"E46.trimOffspring")}),1.0]])]});
            var Q12;
            Q12=makeQuery(id+"F4.imprint","IMPRINT",FACE,{"disambiguationData":[TD([[makeQuery(id+"F4.imprint","IMPRINT",EDGE,{"derivedFrom":sQuery(id+"F4.wireOp",EDGE,"E18")}),-1.0]])]});
            var Q13;
            {var subQ0=sQuery(id+"F4.wireOp",EDGE,"E19.2.left");Q13=makeQuery(id+"F4.imprint","IMPRINT",FACE,{"disambiguationData":[TD([[makeQuery(id+"F4.imprint","IMPRINT",EDGE,{"derivedFrom":subQ0}),1.0]])]});}
            var Q14;
            {var subQ0=sQuery(id+"F4.wireOp",EDGE,"E19.2.right");Q14=makeQuery(id+"F4.imprint","IMPRINT",FACE,{"disambiguationData":[TD([[makeQuery(id+"F4.imprint","IMPRINT",EDGE,{"derivedFrom":subQ0}),-1.0]])]});}
            var Q15;
            {var subQ0=sQuery(id+"F4.wireOp",EDGE,"E21.6.right");Q15=makeQuery(id+"F4.imprint","IMPRINT",FACE,{"disambiguationData":[TD([[makeQuery(id+"F4.imprint","IMPRINT",EDGE,{"derivedFrom":subQ0}),-1.0]])]});}
            var Q16;
            Q16=makeQuery(id+"F4.imprint","IMPRINT",FACE,{"disambiguationData":[TD([[makeQuery(id+"F4.imprint","IMPRINT",EDGE,{"derivedFrom":sQuery(id+"F4.wireOp",EDGE,"E19.3.left")}),1.0]])]});
            var Q17;
            {var subQ0=sQuery(id+"F4.wireOp",EDGE,"E21.1.left");Q17=makeQuery(id+"F4.imprint","IMPRINT",FACE,{"disambiguationData":[TD([[makeQuery(id+"F4.imprint","IMPRINT",EDGE,{"derivedFrom":subQ0}),1.0]])]});}
            var Q18;
            Q18=makeQuery(id+"F4.imprint","IMPRINT",FACE,{"disambiguationData":[TD([[makeQuery(id+"F4.imprint","IMPRINT",EDGE,{"derivedFrom":sQuery(id+"F4.wireOp",EDGE,"E19.1.right")}),-1.0]])]});
            var Q19;
            {var subQ0=sQuery(id+"F4.wireOp",EDGE,"E19.1.left");Q19=makeQuery(id+"F4.imprint","IMPRINT",FACE,{"disambiguationData":[TD([[makeQuery(id+"F4.imprint","IMPRINT",EDGE,{"derivedFrom":subQ0}),1.0]])]});}
            var Q20;
            Q20=makeQuery(id+"F4.imprint","IMPRINT",FACE,{"disambiguationData":[TD([[makeQuery(id+"F4.imprint","IMPRINT",EDGE,{"derivedFrom":sQuery(id+"F4.wireOp",EDGE,"E21.2.right")}),-1.0]])]});
            var Q21;
            Q21=makeQuery(id+"F4.imprint","IMPRINT",FACE,{"disambiguationData":[TD([[makeQuery(id+"F4.imprint","IMPRINT",EDGE,{"derivedFrom":sQuery(id+"F4.wireOp",EDGE,"E22.1.right")}),-1.0]])]});
            var Q22;
            Q22=makeQuery(id+"F4.imprint","IMPRINT",FACE,{"disambiguationData":[TD([[makeQuery(id+"F4.imprint","IMPRINT",EDGE,{"derivedFrom":sQuery(id+"F4.wireOp",EDGE,"E21.3.right")}),-1.0]])]});
            var Q23;
            {var subQ0=sQuery(id+"F4.wireOp",EDGE,"E21.3.left");Q23=makeQuery(id+"F4.imprint","IMPRINT",FACE,{"disambiguationData":[TD([[makeQuery(id+"F4.imprint","IMPRINT",EDGE,{"derivedFrom":subQ0}),1.0]])]});}
            var Q24;
            Q24=makeQuery(id+"F4.imprint","IMPRINT",FACE,{"disambiguationData":[TD([[makeQuery(id+"F4.imprint","IMPRINT",EDGE,{"derivedFrom":sQuery(id+"F4.wireOp",EDGE,"E69.trimOffspring")}),1.0]])]});
            var Q25;
            {var subQ0=sQuery(id+"F4.wireOp",EDGE,"E84.trimOffspring");Q25=makeQuery(id+"F4.imprint","IMPRINT",FACE,{"disambiguationData":[TD([[makeQuery(id+"F4.imprint","IMPRINT",EDGE,{"derivedFrom":subQ0}),-1.0]])]});}
            var Q26;
            Q26=makeQuery(id+"F4.imprint","IMPRINT",FACE,{"disambiguationData":[TD([[makeQuery(id+"F4.imprint","IMPRINT",EDGE,{"derivedFrom":sQuery(id+"F4.wireOp",EDGE,"E71.trimOffspring")}),1.0]])]});
            var Q27;
            {var subQ0=sQuery(id+"F4.wireOp",EDGE,"E88.trimOffspring");Q27=makeQuery(id+"F4.imprint","IMPRINT",FACE,{"disambiguationData":[TD([[makeQuery(id+"F4.imprint","IMPRINT",EDGE,{"derivedFrom":subQ0}),-1.0]])]});}
            var Q28;
            {var subQ0=sQuery(id+"F4.wireOp",EDGE,"E21.4.right");Q28=makeQuery(id+"F4.imprint","IMPRINT",FACE,{"disambiguationData":[TD([[makeQuery(id+"F4.imprint","IMPRINT",EDGE,{"derivedFrom":subQ0}),-1.0]])]});}
            var Q29;
            Q29=makeQuery(id+"F4.imprint","IMPRINT",FACE,{"disambiguationData":[TD([[makeQuery(id+"F4.imprint","IMPRINT",EDGE,{"derivedFrom":sQuery(id+"F4.wireOp",EDGE,"E21.4.left")}),1.0]])]});
            var Q30;
            Q30=makeQuery(id+"F4.imprint","IMPRINT",FACE,{"disambiguationData":[TD([[makeQuery(id+"F4.imprint","IMPRINT",EDGE,{"derivedFrom":sQuery(id+"F4.wireOp",EDGE,"E70.trimOffspring")}),-1.0]])]});
            var Q31;
            Q31=makeQuery(id+"F4.imprint","IMPRINT",FACE,{"disambiguationData":[TD([[makeQuery(id+"F4.imprint","IMPRINT",EDGE,{"derivedFrom":sQuery(id+"F4.wireOp",EDGE,"E21.5.left")}),1.0]])]});
            var Q32;
            {var subQ0=sQuery(id+"F4.wireOp",EDGE,"E19.3.right");Q32=makeQuery(id+"F4.imprint","IMPRINT",FACE,{"disambiguationData":[TD([[makeQuery(id+"F4.imprint","IMPRINT",EDGE,{"derivedFrom":subQ0}),-1.0]])]});}
            var Q33;
            Q33=makeQuery(id+"F4.imprint","IMPRINT",FACE,{"disambiguationData":[TD([[makeQuery(id+"F4.imprint","IMPRINT",EDGE,{"derivedFrom":sQuery(id+"F4.wireOp",EDGE,"E91.bottom")}),-1.0]])]});
            var Q34;
            Q34=makeQuery(id+"F4.imprint","IMPRINT",FACE,{"disambiguationData":[TD([[makeQuery(id+"F4.imprint","IMPRINT",EDGE,{"derivedFrom":sQuery(id+"F4.wireOp",EDGE,"E93")}),1.0]])]});
            var Q35;
            Q35=makeQuery(id+"F4.imprint","IMPRINT",FACE,{"disambiguationData":[TD([[makeQuery(id+"F4.imprint","IMPRINT",EDGE,{"derivedFrom":sQuery(id+"F4.wireOp",EDGE,"E107")}),1.0]])]});
            var Q36;
            Q36=makeQuery(id+"F4.imprint","IMPRINT",FACE,{"disambiguationData":[TD([[makeQuery(id+"F4.imprint","IMPRINT",EDGE,{"derivedFrom":sQuery(id+"F4.wireOp",EDGE,"E90.sketch_text.stroke-0")}),-1.0]])]});
            var Q37;
            Q37=makeQuery(id+"F4.imprint","IMPRINT",FACE,{"disambiguationData":[TD([[makeQuery(id+"F4.imprint","IMPRINT",EDGE,{"derivedFrom":sQuery(id+"F4.wireOp",EDGE,"E90.sketch_text.stroke-12")}),-1.0]])]});
            var Q38;
            Q38=makeQuery(id+"F4.imprint","IMPRINT",FACE,{"disambiguationData":[TD([[makeQuery(id+"F4.imprint","IMPRINT",EDGE,{"derivedFrom":sQuery(id+"F4.wireOp",EDGE,"E90.sketch_text.stroke-22")}),-1.0]])]});
            var Q39;
            Q39=makeQuery(id+"F4.imprint","IMPRINT",FACE,{"disambiguationData":[TD([[makeQuery(id+"F4.imprint","IMPRINT",EDGE,{"derivedFrom":sQuery(id+"F4.wireOp",EDGE,"E90.sketch_text.stroke-40")}),-1.0]])]});
            var Q40;
            Q40=makeQuery(id+"F4.imprint","IMPRINT",FACE,{"disambiguationData":[TD([[makeQuery(id+"F4.imprint","IMPRINT",EDGE,{"derivedFrom":sQuery(id+"F4.wireOp",EDGE,"E90.sketch_text.stroke-47")}),-1.0]])]});
            var Q41;
            Q41=makeQuery(id+"F4.imprint","IMPRINT",FACE,{"disambiguationData":[TD([[makeQuery(id+"F4.imprint","IMPRINT",EDGE,{"derivedFrom":sQuery(id+"F4.wireOp",EDGE,"E90.sketch_text.stroke-65")}),-1.0]])]});
            var Q42;
            Q42=makeQuery(id+"F4.imprint","IMPRINT",FACE,{"disambiguationData":[TD([[makeQuery(id+"F4.imprint","IMPRINT",EDGE,{"derivedFrom":sQuery(id+"F4.wireOp",EDGE,"E90.sketch_text.stroke-83")}),-1.0]])]});
            extrude(context, id + "F5", {"entities" : qUnion([Q0, Q1, Q2, Q3, Q4, Q5, Q6, Q7, Q8, Q9, Q10, Q11, Q12, Q13, Q14, Q15, Q16, Q17, Q18, Q19, Q20, Q21, Q22, Q23, Q24, Q25, Q26, Q27, Q28, Q29, Q30, Q31, Q32, Q33, Q34, Q35, Q36, Q37, Q38, Q39, Q40, Q41, Q42]), "operationType" : NewBodyOperationType.REMOVE, "endBound" : BoundingType.THROUGH_ALL, "oppositeDirection" : true, "depth" : 25 * mm});
        }
    });
